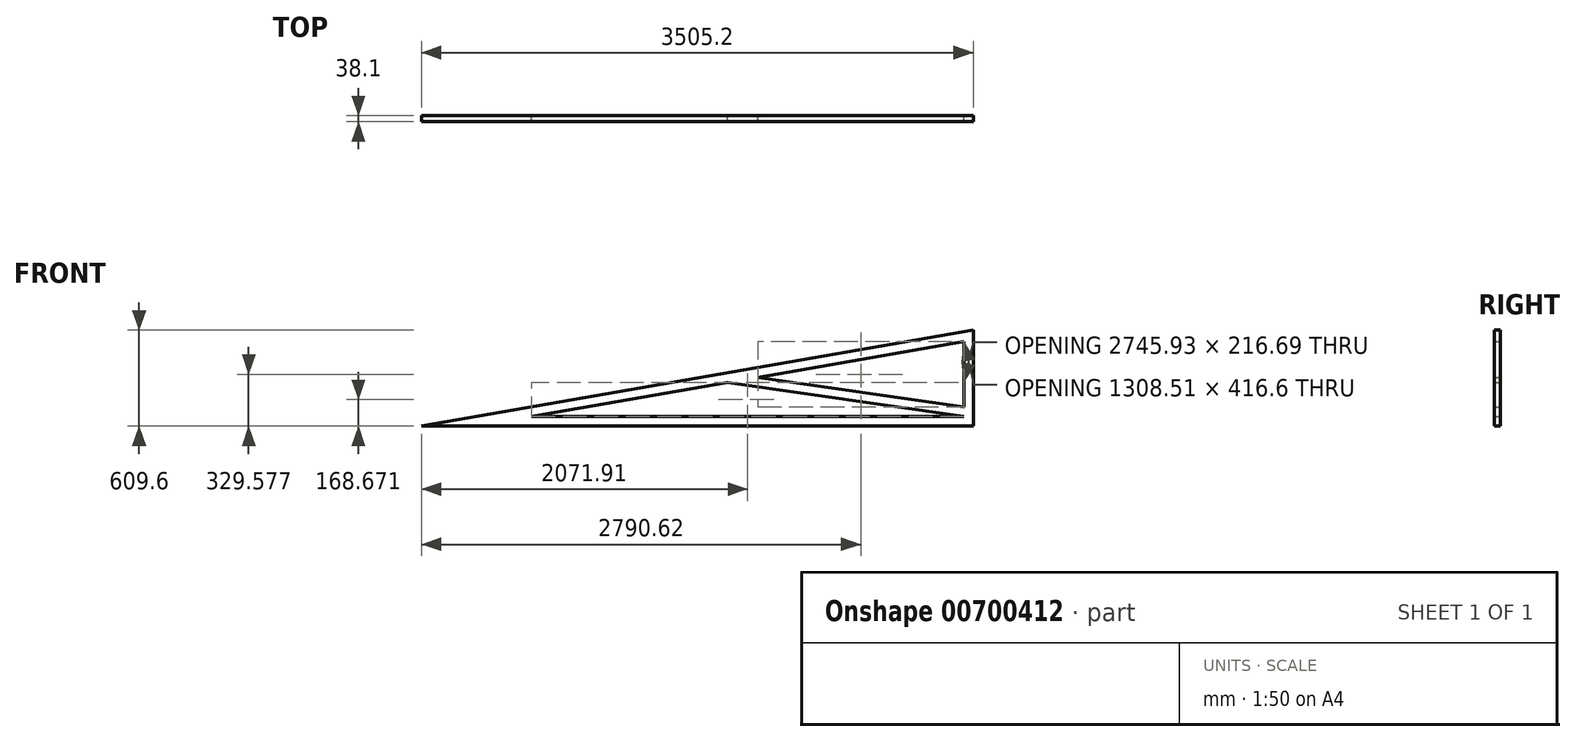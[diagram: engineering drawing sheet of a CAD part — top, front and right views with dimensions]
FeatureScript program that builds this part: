
annotation { "Feature Type Name" : "Feature", "Feature Type Description" : "" }
export const myFeature = defineFeature(function(context is Context, id is Id, definition is map)
    precondition{}
    {
        {
            var Q0;
            Q0=qCreatedBy(makeId("Front.planeOp"),FACE);
            var sketch = newSketch(context, id + "F0", { "sketchPlane" : qUnion([Q0])});
            skLineSegment(sketch, "E0", {"start": v(0, 0) * mm, "end": v(-3505.2, 0) * mm});
            skLineSegment(sketch, "E1", {"start": v(-3505.2, 0) * mm, "end": v(0, 609.6) * mm});
            skLineSegment(sketch, "E2", {"start": v(0, 609.6) * mm, "end": v(0, 0) * mm});
            skLineSegment(sketch, "E3", {"start": v(-1560.28, 277.02) * mm, "end": v(-2806.26, 60.32) * mm});
            skLineSegment(sketch, "E4", {"start": v(-2806.26, 60.32) * mm, "end": v(-60.33, 60.33) * mm});
            skLineSegment(sketch, "E5", {"start": v(-60.33, 60.33) * mm, "end": v(-1560.28, 277.02) * mm});
            skLineSegment(sketch, "E6", {"start": v(-1368.84, 310.31) * mm, "end": v(-60.32, 121.28) * mm});
            skLineSegment(sketch, "E7", {"start": v(-60.33, 121.28) * mm, "end": v(-60.33, 537.88) * mm});
            skLineSegment(sketch, "E8", {"start": v(-60.32, 537.88) * mm, "end": v(-1368.84, 310.31) * mm});
            skLineSegment(sketch, "E9", {"start": v(-1560.28, 277.02) * mm, "end": v(-1752.6, 304.8) * mm, "construction": true});
            skSolve(sketch);
        }
        {
            var Q0;
            Q0 = qSketchRegion(id + "F0", true);
            extrude(context, id + "F1", {"entities" : qUnion([Q0]), "depth" : 38.1 * mm, "offsetDistance" : 25.4 * mm});
        }
    });
